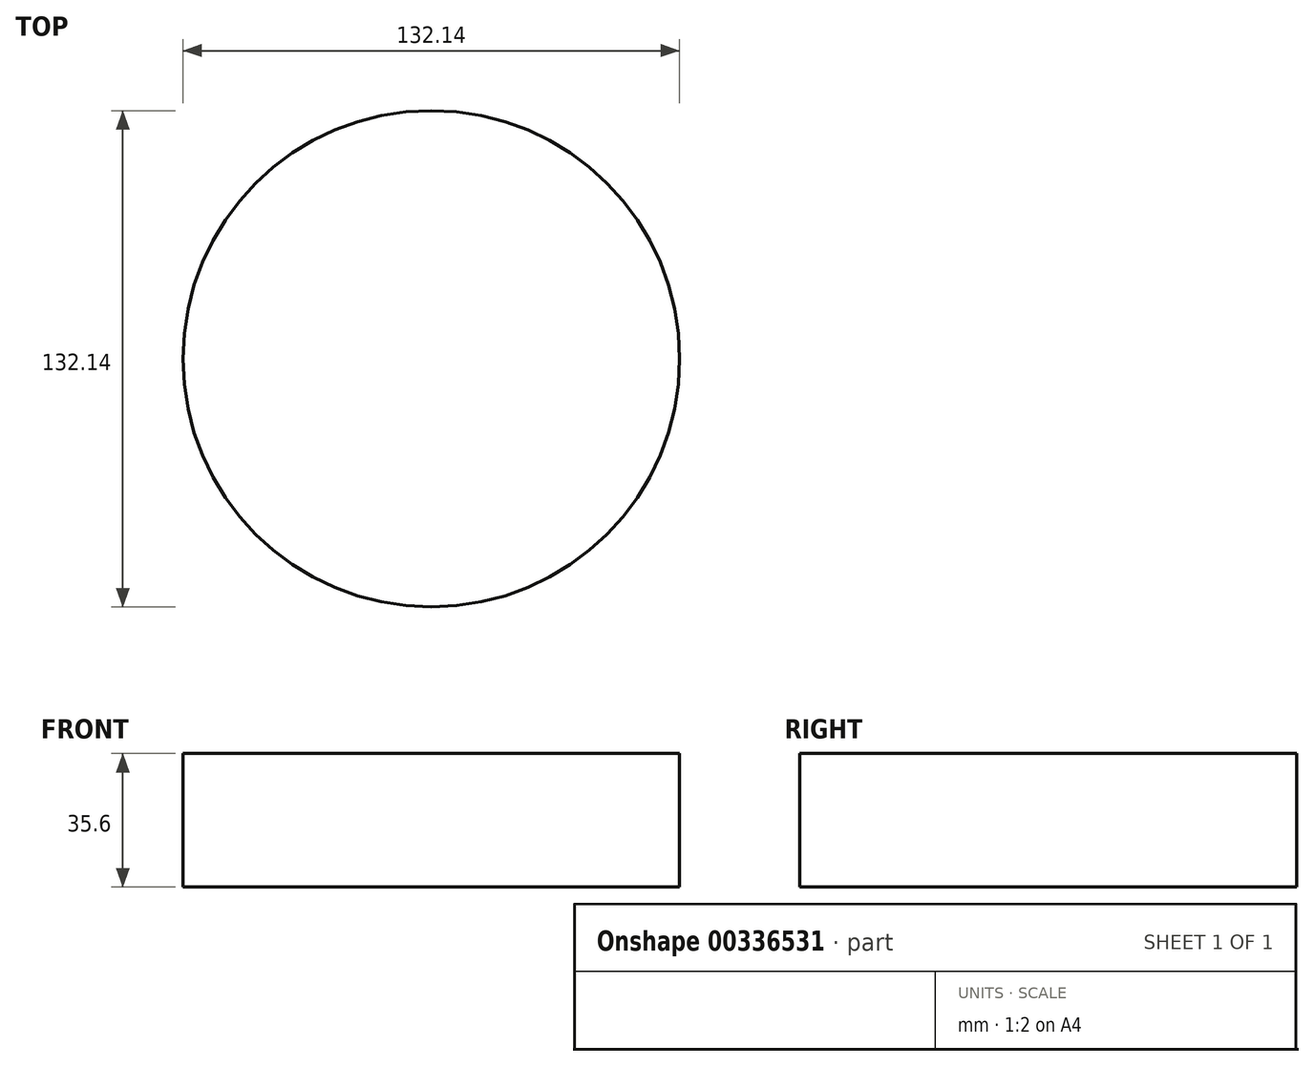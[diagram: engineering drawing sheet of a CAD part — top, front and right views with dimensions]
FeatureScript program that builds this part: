
annotation { "Feature Type Name" : "Feature", "Feature Type Description" : "" }
export const myFeature = defineFeature(function(context is Context, id is Id, definition is map)
    precondition{}
    {
        {
            var Q0;
            Q0=qCreatedBy(makeId("Top.planeOp"),FACE);
            var sketch = newSketch(context, id + "F0", { "sketchPlane" : qUnion([Q0])});
            skCircle(sketch, "E0", {"center": v(0, 0) * mm, "radius": 41.56 * mm});
            skCircle(sketch, "E1", {"center": v(0, 0) * mm, "radius": 66.07 * mm});
            skSolve(sketch);
        }
        {
            var Q0;
            Q0=sQuery(id+"F0.wireOp",EDGE,"E1");
            extrude(context, id + "F1", {"bodyType" : ToolBodyType.SURFACE, "surfaceEntities" : qUnion([Q0]), "depth" : 35.6 * mm});
        }
    });
